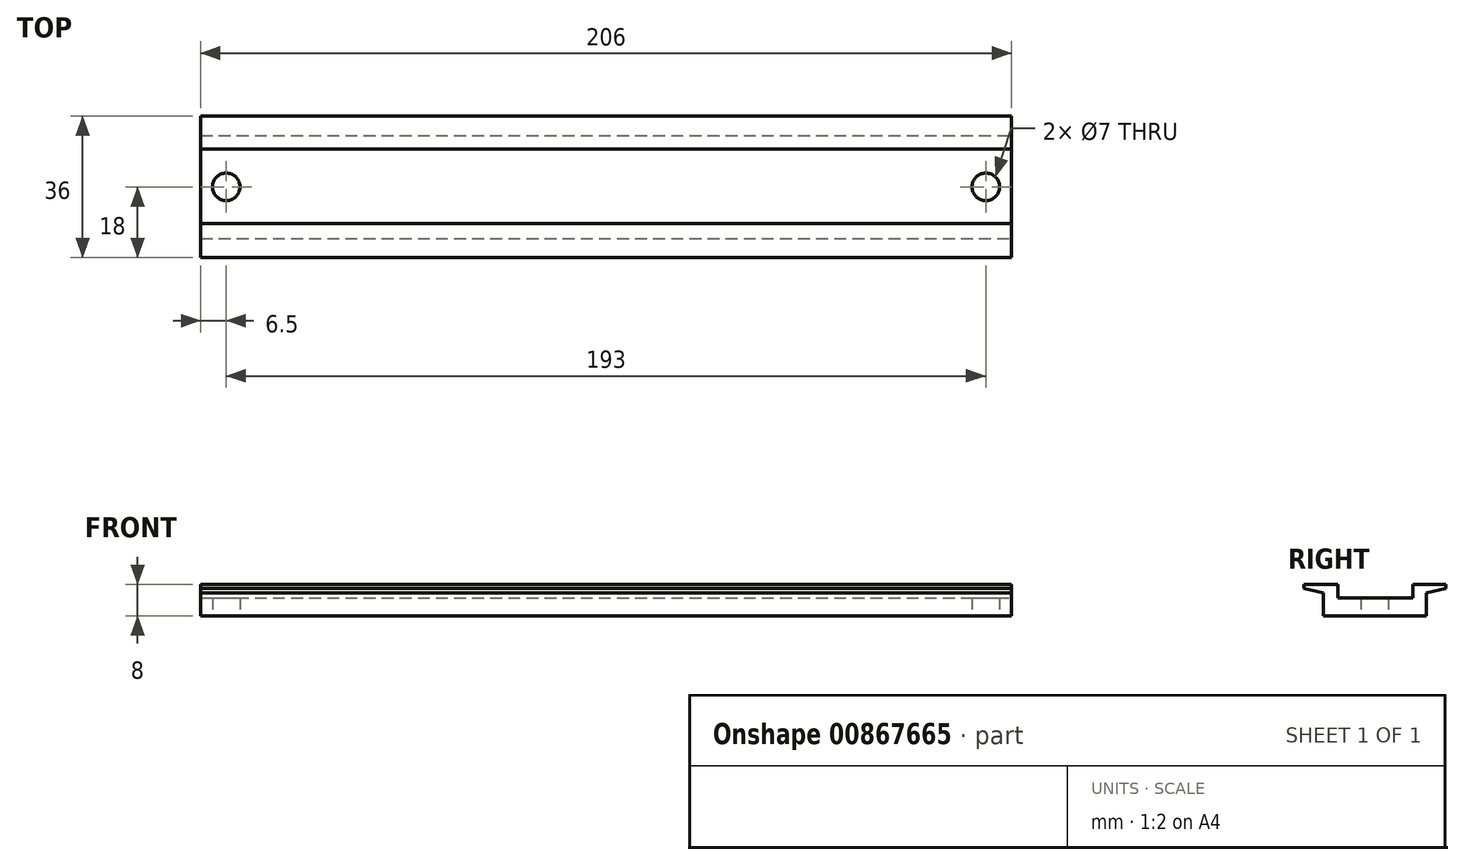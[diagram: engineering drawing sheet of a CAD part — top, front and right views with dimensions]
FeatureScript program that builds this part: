
annotation { "Feature Type Name" : "Feature", "Feature Type Description" : "" }
export const myFeature = defineFeature(function(context is Context, id is Id, definition is map)
    precondition{}
    {
        {
            var Q0;
            Q0=qCreatedBy(makeId("Top.planeOp"),FACE);
            var sketch = newSketch(context, id + "F0", { "sketchPlane" : qUnion([Q0])});
            skLineSegment(sketch, "E0.bottom", {"start": v(-103, 18) * mm, "end": v(103, 18) * mm});
            skLineSegment(sketch, "E0.top", {"start": v(-103, -18) * mm, "end": v(103, -18) * mm});
            skLineSegment(sketch, "E0.left", {"start": v(-103, 18) * mm, "end": v(-103, -18) * mm});
            skLineSegment(sketch, "E0.right", {"start": v(103, 18) * mm, "end": v(103, -18) * mm});
            skPoint(sketch, "E0.middle", {"position": v(0, 0) * mm});
            skPoint(sketch, "E1", {"position": v(-96.5, 0) * mm});
            skPoint(sketch, "E2.MirrorP", {"position": v(96.5, 0) * mm});
            skCircle(sketch, "E3", {"center": v(96.5, 0) * mm, "radius": 3.5 * mm});
            skCircle(sketch, "E4.MirrorC", {"center": v(-96.5, 0) * mm, "radius": 3.5 * mm});
            skSolve(sketch);
        }
        {
            var Q0;
            Q0=makeQuery(id+"F0.imprint","IMPRINT",FACE,{"disambiguationData":[TD([[makeQuery(id+"F0.imprint","IMPRINT",EDGE,{"derivedFrom":sQuery(id+"F0.wireOp",EDGE,"E0.bottom")}),-1.0]])]});
            extrude(context, id + "F1", {"entities" : qUnion([Q0]), "depth" : 8 * mm, "offsetDistance" : 25 * mm});
        }
        {
            var Q0;
            Q0=makeQuery(id+"F1.opExtrude","SWEPT_FACE",FACE,{"disambiguationData":[OSD([sQuery(id+"F0.wireOp",EDGE,"E0.right")])]});
            var sketch = newSketch(context, id + "F2", { "sketchPlane" : qUnion([Q0])});
            skLineSegment(sketch, "E5.bottom", {"start": v(-9.37, 8) * mm, "end": v(9.65, 8) * mm});
            skLineSegment(sketch, "E5.top", {"start": v(-9.37, 4.6) * mm, "end": v(9.65, 4.6) * mm});
            skLineSegment(sketch, "E5.left", {"start": v(-9.37, 8) * mm, "end": v(-9.37, 4.6) * mm});
            skLineSegment(sketch, "E5.right", {"start": v(9.65, 8) * mm, "end": v(9.65, 4.6) * mm});
            skSolve(sketch);
        }
        {
            var Q0;
            Q0=makeQuery(id+"F2.imprint","IMPRINT",FACE,{"disambiguationData":[TD([[makeQuery(id+"F2.imprint","IMPRINT",EDGE,{"derivedFrom":sQuery(id+"F2.wireOp",EDGE,"E5.bottom")}),1.0]])]});
            extrude(context, id + "F3", {"entities" : qUnion([Q0]), "operationType" : NewBodyOperationType.REMOVE, "endBound" : BoundingType.THROUGH_ALL, "oppositeDirection" : true, "depth" : 192 * mm, "offsetDistance" : 25 * mm});
        }
        {
            var Q0;
            Q0=makeQuery(id+"F1.opExtrude","SWEPT_FACE",FACE,{"disambiguationData":[OSD([sQuery(id+"F0.wireOp",EDGE,"E0.right")])]});
            var sketch = newSketch(context, id + "F4", { "sketchPlane" : qUnion([Q0])});
            skLineSegment(sketch, "E6", {"start": v(-18, 6.97) * mm, "end": v(-13.1, 5.89) * mm});
            skLineSegment(sketch, "E7", {"start": v(-13.1, 5.89) * mm, "end": v(-13.1, 0) * mm});
            skLineSegment(sketch, "E8.MirrorCS", {"start": v(18, 6.97) * mm, "end": v(13.1, 5.89) * mm});
            skLineSegment(sketch, "E9.MirrorCS", {"start": v(13.1, 5.89) * mm, "end": v(13.1, 0) * mm});
            skSolve(sketch);
        }
        {
            var Q0;
            {var subQ0=sQuery(id+"F4.wireOp",EDGE,"E8.MirrorCS");Q0=makeQuery(id+"F4.imprint","IMPRINT",FACE,{"disambiguationData":[TD([[makeQuery(id+"F4.imprint","IMPRINT",EDGE,{"derivedFrom":subQ0}),1.0]])]});}
            var Q1;
            {var subQ0=sQuery(id+"F4.wireOp",EDGE,"E6");Q1=makeQuery(id+"F4.imprint","IMPRINT",FACE,{"disambiguationData":[TD([[makeQuery(id+"F4.imprint","IMPRINT",EDGE,{"derivedFrom":subQ0}),-1.0]])]});}
            extrude(context, id + "F5", {"entities" : qUnion([Q0, Q1]), "operationType" : NewBodyOperationType.REMOVE, "endBound" : BoundingType.THROUGH_ALL, "oppositeDirection" : true, "depth" : 25 * mm, "offsetDistance" : 25 * mm});
        }
    });
